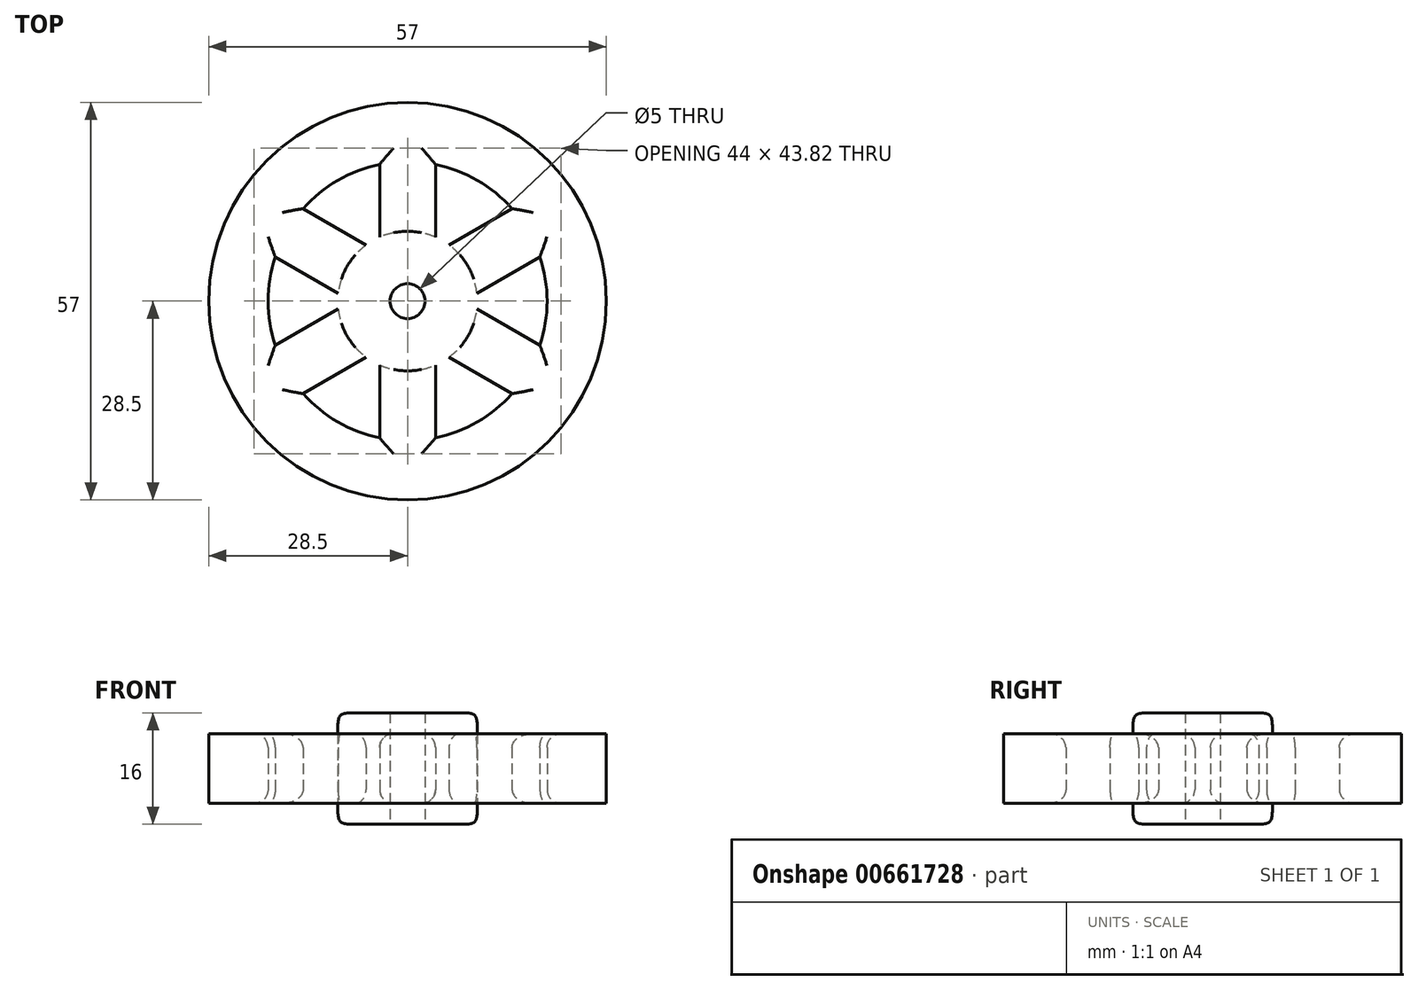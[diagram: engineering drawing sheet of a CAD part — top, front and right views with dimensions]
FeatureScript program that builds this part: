
annotation { "Feature Type Name" : "Feature", "Feature Type Description" : "" }
export const myFeature = defineFeature(function(context is Context, id is Id, definition is map)
    precondition{}
    {
        {
            var Q0;
            Q0=qCreatedBy(makeId("Top.planeOp"),FACE);
            var sketch = newSketch(context, id + "F0", { "sketchPlane" : qUnion([Q0])});
            skCircle(sketch, "E0", {"center": v(0, 0) * mm, "radius": 2.5 * mm});
            skArc(sketch, "E1", {"start": v(-4, 9.17) * mm, "mid": v(-5, 8.66) * mm, "end": v(-5.94, 8.05) * mm});
            skCircle(sketch, "E2", {"center": v(0, 0) * mm, "radius": 28.5 * mm});
            skLineSegment(sketch, "E3", {"start": v(-4, 9.17) * mm, "end": v(-4, 19.6) * mm});
            skLineSegment(sketch, "E4", {"start": v(4, 9.17) * mm, "end": v(4, 19.6) * mm});
            skLineSegment(sketch, "E5.1.0", {"start": v(-9.94, 1.12) * mm, "end": v(-18.97, 6.33) * mm});
            skLineSegment(sketch, "E5.1.1", {"start": v(-5.94, 8.05) * mm, "end": v(-14.97, 13.26) * mm});
            skLineSegment(sketch, "E5.2.0", {"start": v(-5.94, -8.05) * mm, "end": v(-14.97, -13.26) * mm});
            skLineSegment(sketch, "E5.2.1", {"start": v(-9.94, -1.12) * mm, "end": v(-18.97, -6.33) * mm});
            skLineSegment(sketch, "E5.3.0", {"start": v(4, -9.17) * mm, "end": v(4, -19.6) * mm});
            skLineSegment(sketch, "E5.3.1", {"start": v(-4, -9.17) * mm, "end": v(-4, -19.6) * mm});
            skLineSegment(sketch, "E5.4.0", {"start": v(9.94, -1.12) * mm, "end": v(18.97, -6.33) * mm});
            skLineSegment(sketch, "E5.4.1", {"start": v(5.94, -8.05) * mm, "end": v(14.97, -13.26) * mm});
            skLineSegment(sketch, "E5.5.0", {"start": v(5.94, 8.05) * mm, "end": v(14.97, 13.26) * mm});
            skLineSegment(sketch, "E5.5.1", {"start": v(9.94, 1.12) * mm, "end": v(18.97, 6.33) * mm});
            skArc(sketch, "E6.trimOffspring", {"start": v(-9.94, 1.12) * mm, "mid": v(-10, 0) * mm, "end": v(-9.94, -1.12) * mm});
            skArc(sketch, "E7.trimOffspring", {"start": v(-5.94, -8.05) * mm, "mid": v(-5, -8.66) * mm, "end": v(-4, -9.17) * mm});
            skArc(sketch, "E8.trimOffspring", {"start": v(4, -9.17) * mm, "mid": v(5, -8.66) * mm, "end": v(5.94, -8.05) * mm});
            skArc(sketch, "E9.trimOffspring", {"start": v(9.94, -1.12) * mm, "mid": v(10, 0) * mm, "end": v(9.94, 1.12) * mm});
            skArc(sketch, "E10.trimOffspring", {"start": v(5.94, 8.05) * mm, "mid": v(5, 8.66) * mm, "end": v(4, 9.17) * mm});
            skArc(sketch, "E11", {"start": v(-4, 19.6) * mm, "mid": v(-10, 17.32) * mm, "end": v(-14.97, 13.26) * mm});
            skPoint(sketch, "E12.orphan", {"position": v(-4, 28.22) * mm});
            skPoint(sketch, "E13.orphan", {"position": v(4, 28.22) * mm});
            skPoint(sketch, "E14.orphan", {"position": v(22.44, 17.57) * mm});
            skArc(sketch, "E15.trimOffspring", {"start": v(14.97, 13.26) * mm, "mid": v(10, 17.32) * mm, "end": v(4, 19.6) * mm});
            skPoint(sketch, "E16.orphan", {"position": v(26.44, 10.64) * mm});
            skPoint(sketch, "E17.orphan", {"position": v(26.44, -10.64) * mm});
            skPoint(sketch, "E18.orphan", {"position": v(22.44, -17.57) * mm});
            skArc(sketch, "E19.trimOffspring", {"start": v(18.97, -6.33) * mm, "mid": v(20, 0) * mm, "end": v(18.97, 6.33) * mm});
            skArc(sketch, "E20.trimOffspring", {"start": v(4, -19.6) * mm, "mid": v(10, -17.32) * mm, "end": v(14.97, -13.26) * mm});
            skPoint(sketch, "E21.orphan", {"position": v(-4, -28.22) * mm});
            skPoint(sketch, "E22.orphan", {"position": v(4, -28.22) * mm});
            skArc(sketch, "E23.trimOffspring", {"start": v(-14.97, -13.26) * mm, "mid": v(-10, -17.32) * mm, "end": v(-4, -19.6) * mm});
            skPoint(sketch, "E24.orphan", {"position": v(-22.44, -17.57) * mm});
            skPoint(sketch, "E25.orphan", {"position": v(-26.44, -10.64) * mm});
            skPoint(sketch, "E26.orphan", {"position": v(-26.44, 10.64) * mm});
            skPoint(sketch, "E27.orphan", {"position": v(-22.44, 17.57) * mm});
            skArc(sketch, "E28.trimOffspring", {"start": v(-18.97, 6.33) * mm, "mid": v(-20, 0) * mm, "end": v(-18.97, -6.33) * mm});
            skCircle(sketch, "E29", {"center": v(0, 0) * mm, "radius": 10 * mm});
            skSolve(sketch);
        }
        {
            var Q0;
            Q0=makeQuery(id+"F0.imprint","IMPRINT",FACE,{"disambiguationData":[TD([[makeQuery(id+"F0.imprint","IMPRINT",EDGE,{"derivedFrom":sQuery(id+"F0.wireOp",EDGE,"E0")}),-1.0]])]});
            extrude(context, id + "F1", {"entities" : qUnion([Q0]), "endBound" : BoundingType.SYMMETRIC, "depth" : 16 * mm, "offsetDistance" : 25 * mm});
        }
        {
            var Q0;
            Q0=makeQuery(id+"F0.imprint","IMPRINT",FACE,{"disambiguationData":[TD([[makeQuery(id+"F0.imprint","IMPRINT",EDGE,{"derivedFrom":sQuery(id+"F0.wireOp",EDGE,"E2")}),1.0]])]});
            extrude(context, id + "F2", {"entities" : qUnion([Q0]), "operationType" : NewBodyOperationType.ADD, "endBound" : BoundingType.SYMMETRIC, "depth" : 10 * mm, "offsetDistance" : 25 * mm});
        }
        {
            var Q0;
            Q0=makeQuery(id+"F1.opExtrude","CAP_EDGE",EDGE,{"disambiguationData":[OSD([sQuery(id+"F0.wireOp",EDGE,"E29")])],"isStart":false});
            var Q1;
            Q1=makeQuery(id+"F1.opExtrude","CAP_EDGE",EDGE,{"disambiguationData":[OSD([sQuery(id+"F0.wireOp",EDGE,"E29")])],"isStart":true});
            fillet(context, id + "F3", {"entities" : qUnion([Q0, Q1]), "radius" : 2.5 * mm, "tangentPropagation" : true, "rho" : 0.7, "crossSection" : FilletCrossSection.CONIC, "allowEdgeOverflow" : false});
        }
        {
            var Q0;
            Q0=makeQuery(id+"F2.opExtrude","CAP_EDGE",EDGE,{"disambiguationData":[OSD([sQuery(id+"F0.wireOp",EDGE,"E28.trimOffspring")])],"isStart":false});
            var Q1;
            Q1=makeQuery(id+"F2.opExtrude","CAP_EDGE",EDGE,{"disambiguationData":[OSD([sQuery(id+"F0.wireOp",EDGE,"E5.2.1")])],"isStart":false});
            var Q2;
            Q2=makeQuery(id+"F2.opExtrude","CAP_EDGE",EDGE,{"disambiguationData":[OSD([sQuery(id+"F0.wireOp",EDGE,"E5.1.0")])],"isStart":false});
            var Q3;
            Q3=makeQuery(id+"F2.opExtrude","CAP_EDGE",EDGE,{"disambiguationData":[OSD([sQuery(id+"F0.wireOp",EDGE,"E5.1.1")])],"isStart":false});
            var Q4;
            Q4=makeQuery(id+"F2.opExtrude","CAP_EDGE",EDGE,{"disambiguationData":[OSD([sQuery(id+"F0.wireOp",EDGE,"E11")])],"isStart":false});
            var Q5;
            Q5=makeQuery(id+"F2.opExtrude","CAP_EDGE",EDGE,{"disambiguationData":[OSD([sQuery(id+"F0.wireOp",EDGE,"E3")])],"isStart":false});
            var Q6;
            Q6=makeQuery(id+"F2.opExtrude","CAP_EDGE",EDGE,{"disambiguationData":[OSD([sQuery(id+"F0.wireOp",EDGE,"E4")])],"isStart":false});
            var Q7;
            Q7=makeQuery(id+"F2.opExtrude","CAP_EDGE",EDGE,{"disambiguationData":[OSD([sQuery(id+"F0.wireOp",EDGE,"E15.trimOffspring")])],"isStart":false});
            var Q8;
            Q8=makeQuery(id+"F2.opExtrude","CAP_EDGE",EDGE,{"disambiguationData":[OSD([sQuery(id+"F0.wireOp",EDGE,"E5.5.0")])],"isStart":false});
            var Q9;
            Q9=makeQuery(id+"F2.opExtrude","CAP_EDGE",EDGE,{"disambiguationData":[OSD([sQuery(id+"F0.wireOp",EDGE,"E5.5.1")])],"isStart":false});
            var Q10;
            Q10=makeQuery(id+"F2.opExtrude","CAP_EDGE",EDGE,{"disambiguationData":[OSD([sQuery(id+"F0.wireOp",EDGE,"E5.4.0")])],"isStart":false});
            var Q11;
            Q11=makeQuery(id+"F2.opExtrude","CAP_EDGE",EDGE,{"disambiguationData":[OSD([sQuery(id+"F0.wireOp",EDGE,"E19.trimOffspring")])],"isStart":false});
            var Q12;
            Q12=makeQuery(id+"F2.opExtrude","CAP_EDGE",EDGE,{"disambiguationData":[OSD([sQuery(id+"F0.wireOp",EDGE,"E20.trimOffspring")])],"isStart":false});
            var Q13;
            Q13=makeQuery(id+"F2.opExtrude","CAP_EDGE",EDGE,{"disambiguationData":[OSD([sQuery(id+"F0.wireOp",EDGE,"E5.3.0")])],"isStart":false});
            var Q14;
            Q14=makeQuery(id+"F2.opExtrude","CAP_EDGE",EDGE,{"disambiguationData":[OSD([sQuery(id+"F0.wireOp",EDGE,"E5.3.1")])],"isStart":false});
            var Q15;
            Q15=makeQuery(id+"F2.opExtrude","CAP_EDGE",EDGE,{"disambiguationData":[OSD([sQuery(id+"F0.wireOp",EDGE,"E5.2.0")])],"isStart":false});
            var Q16;
            Q16=makeQuery(id+"F2.opExtrude","CAP_EDGE",EDGE,{"disambiguationData":[OSD([sQuery(id+"F0.wireOp",EDGE,"E23.trimOffspring")])],"isStart":false});
            var Q17;
            Q17=makeQuery(id+"F2.opExtrude","CAP_EDGE",EDGE,{"disambiguationData":[OSD([sQuery(id+"F0.wireOp",EDGE,"E11")])],"isStart":true});
            var Q18;
            Q18=makeQuery(id+"F2.opExtrude","CAP_EDGE",EDGE,{"disambiguationData":[OSD([sQuery(id+"F0.wireOp",EDGE,"E3")])],"isStart":true});
            var Q19;
            Q19=makeQuery(id+"F2.opExtrude","CAP_EDGE",EDGE,{"disambiguationData":[OSD([sQuery(id+"F0.wireOp",EDGE,"E5.1.1")])],"isStart":true});
            var Q20;
            Q20=makeQuery(id+"F2.opExtrude","CAP_EDGE",EDGE,{"disambiguationData":[OSD([sQuery(id+"F0.wireOp",EDGE,"E15.trimOffspring")])],"isStart":true});
            var Q21;
            Q21=makeQuery(id+"F2.opExtrude","CAP_EDGE",EDGE,{"disambiguationData":[OSD([sQuery(id+"F0.wireOp",EDGE,"E4")])],"isStart":true});
            var Q22;
            Q22=makeQuery(id+"F2.opExtrude","CAP_EDGE",EDGE,{"disambiguationData":[OSD([sQuery(id+"F0.wireOp",EDGE,"E5.5.0")])],"isStart":true});
            var Q23;
            Q23=makeQuery(id+"F2.opExtrude","CAP_EDGE",EDGE,{"disambiguationData":[OSD([sQuery(id+"F0.wireOp",EDGE,"E5.5.1")])],"isStart":true});
            var Q24;
            Q24=makeQuery(id+"F2.opExtrude","CAP_EDGE",EDGE,{"disambiguationData":[OSD([sQuery(id+"F0.wireOp",EDGE,"E19.trimOffspring")])],"isStart":true});
            var Q25;
            Q25=makeQuery(id+"F2.opExtrude","CAP_EDGE",EDGE,{"disambiguationData":[OSD([sQuery(id+"F0.wireOp",EDGE,"E5.4.0")])],"isStart":true});
            var Q26;
            Q26=makeQuery(id+"F2.opExtrude","CAP_EDGE",EDGE,{"disambiguationData":[OSD([sQuery(id+"F0.wireOp",EDGE,"E5.4.1")])],"isStart":true});
            var Q27;
            Q27=makeQuery(id+"F2.opExtrude","CAP_EDGE",EDGE,{"disambiguationData":[OSD([sQuery(id+"F0.wireOp",EDGE,"E5.3.0")])],"isStart":true});
            var Q28;
            Q28=makeQuery(id+"F2.opExtrude","CAP_EDGE",EDGE,{"disambiguationData":[OSD([sQuery(id+"F0.wireOp",EDGE,"E20.trimOffspring")])],"isStart":true});
            var Q29;
            Q29=makeQuery(id+"F2.opExtrude","CAP_EDGE",EDGE,{"disambiguationData":[OSD([sQuery(id+"F0.wireOp",EDGE,"E5.3.1")])],"isStart":true});
            var Q30;
            Q30=makeQuery(id+"F2.opExtrude","CAP_EDGE",EDGE,{"disambiguationData":[OSD([sQuery(id+"F0.wireOp",EDGE,"E5.2.0")])],"isStart":true});
            var Q31;
            Q31=makeQuery(id+"F2.opExtrude","CAP_EDGE",EDGE,{"disambiguationData":[OSD([sQuery(id+"F0.wireOp",EDGE,"E23.trimOffspring")])],"isStart":true});
            var Q32;
            Q32=makeQuery(id+"F2.opExtrude","CAP_EDGE",EDGE,{"disambiguationData":[OSD([sQuery(id+"F0.wireOp",EDGE,"E28.trimOffspring")])],"isStart":true});
            var Q33;
            Q33=makeQuery(id+"F2.opExtrude","CAP_EDGE",EDGE,{"disambiguationData":[OSD([sQuery(id+"F0.wireOp",EDGE,"E5.1.0")])],"isStart":true});
            var Q34;
            Q34=makeQuery(id+"F2.opExtrude","CAP_EDGE",EDGE,{"disambiguationData":[OSD([sQuery(id+"F0.wireOp",EDGE,"E5.2.1")])],"isStart":true});
            var Q35;
            Q35=makeQuery(id+"F2.opExtrude","CAP_EDGE",EDGE,{"disambiguationData":[OSD([sQuery(id+"F0.wireOp",EDGE,"E5.4.1")])],"isStart":false});
            fillet(context, id + "F4", {"entities" : qUnion([Q0, Q1, Q2, Q3, Q4, Q5, Q6, Q7, Q8, Q9, Q10, Q11, Q12, Q13, Q14, Q15, Q16, Q17, Q18, Q19, Q20, Q21, Q22, Q23, Q24, Q25, Q26, Q27, Q28, Q29, Q30, Q31, Q32, Q33, Q34, Q35]), "radius" : 2 * mm, "tangentPropagation" : true, "allowEdgeOverflow" : false});
        }
    });
